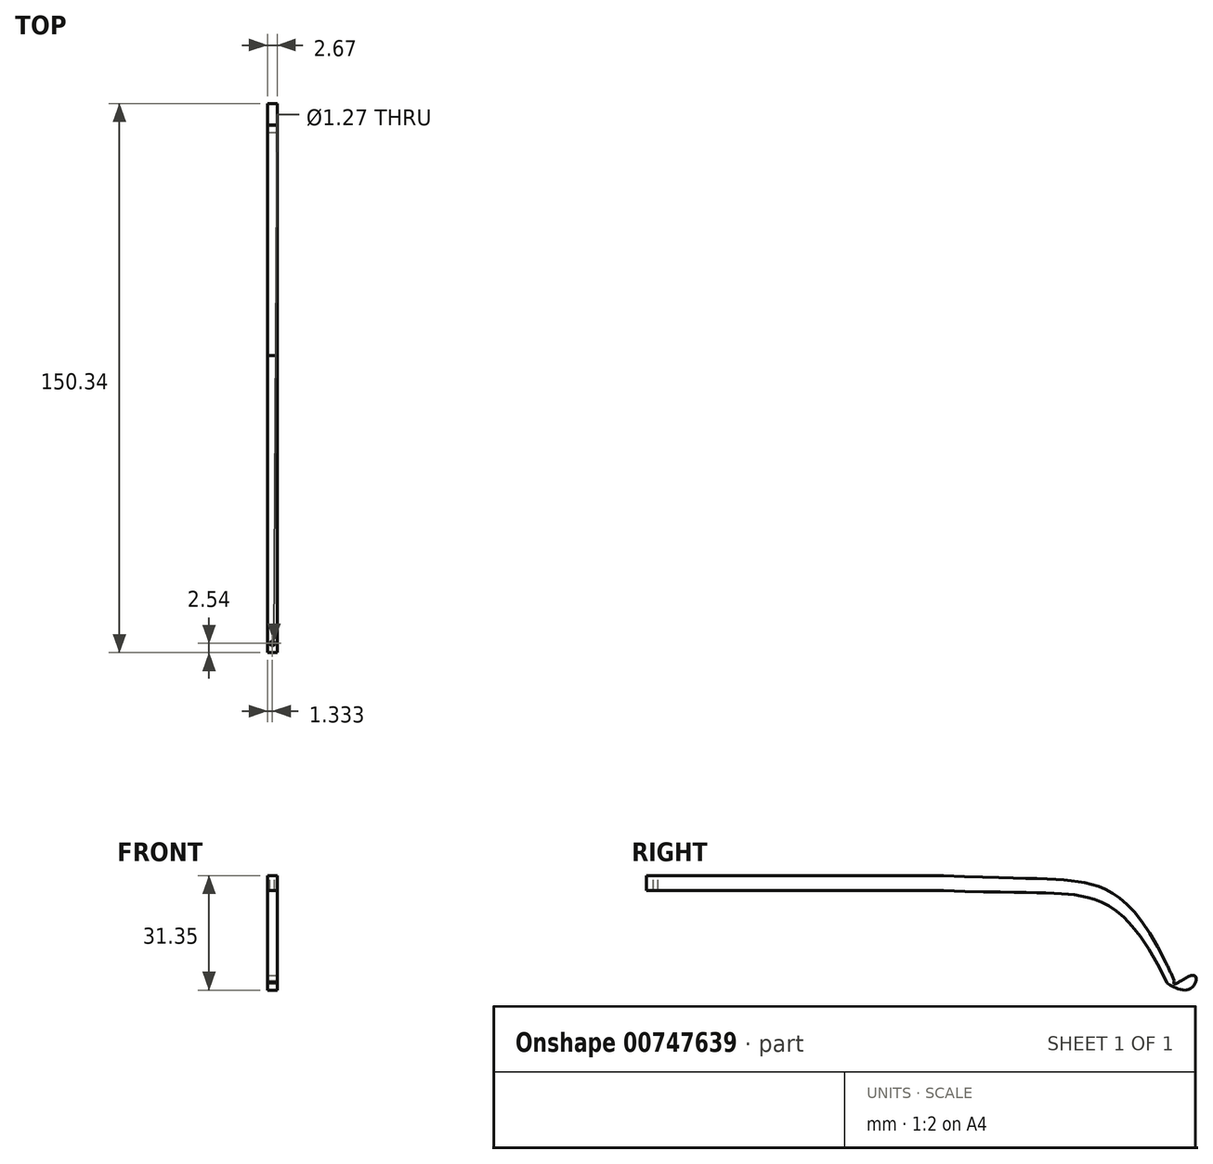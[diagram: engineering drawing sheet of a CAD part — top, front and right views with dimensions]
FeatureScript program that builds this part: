
annotation { "Feature Type Name" : "Feature", "Feature Type Description" : "" }
export const myFeature = defineFeature(function(context is Context, id is Id, definition is map)
    precondition{}
    {
        {
            var Q0;
            Q0=qCreatedBy(makeId("Right.planeOp"),FACE);
            var sketch = newSketch(context, id + "F0", { "sketchPlane" : qUnion([Q0])});
            skLineSegment(sketch, "E0.bottom", {"start": v(-40.64, 2.06) * mm, "end": v(40.64, 2.06) * mm});
            skLineSegment(sketch, "E0.top", {"start": v(-40.64, -2.06) * mm, "end": v(40.64, -2.06) * mm});
            skLineSegment(sketch, "E0.left", {"start": v(-40.64, 2.06) * mm, "end": v(-40.64, -2.06) * mm});
            skPoint(sketch, "E0.middle", {"position": v(0, 0) * mm});
            skFitSpline(sketch, "E1", {"points": [v(40.64, 2.06) * mm, v(79.74, 0) * mm, v(103.8, -26.85) * mm], "startDerivative": vector(143.66, -7) * mm, "endDerivative": vector(57.16, -130.9) * mm});
            skFitSpline(sketch, "E2", {"points": [v(40.64, -2.06) * mm, v(77.83, -3.45) * mm, v(101.66, -27.17) * mm], "startDerivative": vector(143.94, -4.83) * mm, "endDerivative": vector(57.98, -122.16) * mm});
            skFitSpline(sketch, "E3", {"points": [v(103.8, -26.85) * mm, v(108.92, -25.21) * mm, v(108.1, -28.94) * mm, v(101.66, -27.17) * mm], "startDerivative": vector(-11.32, -21.42) * mm, "endDerivative": vector(-6.8, 6.18) * mm});
            skArc(sketch, "E4.filletArc", {"start": v(101.49, -21.84) * mm, "mid": v(104.45, -24.78) * mm, "end": v(108.6, -25.25) * mm});
            skSolve(sketch);
        }
        {
            var Q0;
            Q0=makeQuery(id+"F0.imprint","IMPRINT",FACE,{"disambiguationData":[TD([[makeQuery(id+"F0.imprint","IMPRINT",EDGE,{"derivedFrom":sQuery(id+"F0.wireOp",EDGE,"E0.bottom")}),-1.0]])]});
            var Q1;
            Q1=makeQuery(id+"F0.imprint","IMPRINT",FACE,{"disambiguationData":[TD([[makeQuery(id+"F0.imprint","IMPRINT",EDGE,{"derivedFrom":sQuery(id+"F0.wireOp",EDGE,"E0.right")}),1.0]])]});
            extrude(context, id + "F1", {"entities" : qUnion([Q0, Q1]), "depth" : 2.67 * mm, "offsetDistance" : 25.4 * mm});
        }
        {
            var Q0;
            Q0=makeQuery(id+"F1.opExtrude","SWEPT_FACE",FACE,{"disambiguationData":[OSD([sQuery(id+"F0.wireOp",EDGE,"E0.bottom")])]});
            var sketch = newSketch(context, id + "F2", { "sketchPlane" : qUnion([Q0])});
            skLineSegment(sketch, "E5", {"start": v(0, -38.1) * mm, "end": v(2.67, -38.1) * mm});
            skCircle(sketch, "E6", {"center": v(1.33, -38.1) * mm, "radius": 0.64 * mm});
            skSolve(sketch);
        }
        {
            var Q0;
            {var subQ0=sQuery(id+"F2.wireOp",EDGE,"E6");var subQ1=sQuery(id+"F2.wireOp",EDGE,"E5");var subQ2=makeQuery(id+"F2.imprint","INTERSECT",VERTEX,{"disambiguationData":[OD(0.0)],"derivedFrom":[subQ1,subQ0]});Q0=makeQuery(id+"F2.imprint","IMPRINT",FACE,{"disambiguationData":[TD([[makeQuery(id+"F2.imprint","IMPRINT",EDGE,{"disambiguationData":[TD([[subQ2,-1.0]])],"derivedFrom":subQ1}),1.0]])]});}
            var Q1;
            {var subQ0=sQuery(id+"F2.wireOp",EDGE,"E6");var subQ1=sQuery(id+"F2.wireOp",EDGE,"E5");var subQ2=makeQuery(id+"F2.imprint","INTERSECT",VERTEX,{"disambiguationData":[OD(0.0)],"derivedFrom":[subQ1,subQ0]});Q1=makeQuery(id+"F2.imprint","IMPRINT",FACE,{"disambiguationData":[TD([[makeQuery(id+"F2.imprint","IMPRINT",EDGE,{"disambiguationData":[TD([[subQ2,-1.0]])],"derivedFrom":subQ1}),-1.0]])]});}
            extrude(context, id + "F3", {"entities" : qUnion([Q0, Q1]), "operationType" : NewBodyOperationType.REMOVE, "oppositeDirection" : true, "depth" : 7.62 * mm, "offsetDistance" : 25.4 * mm});
        }
    });
